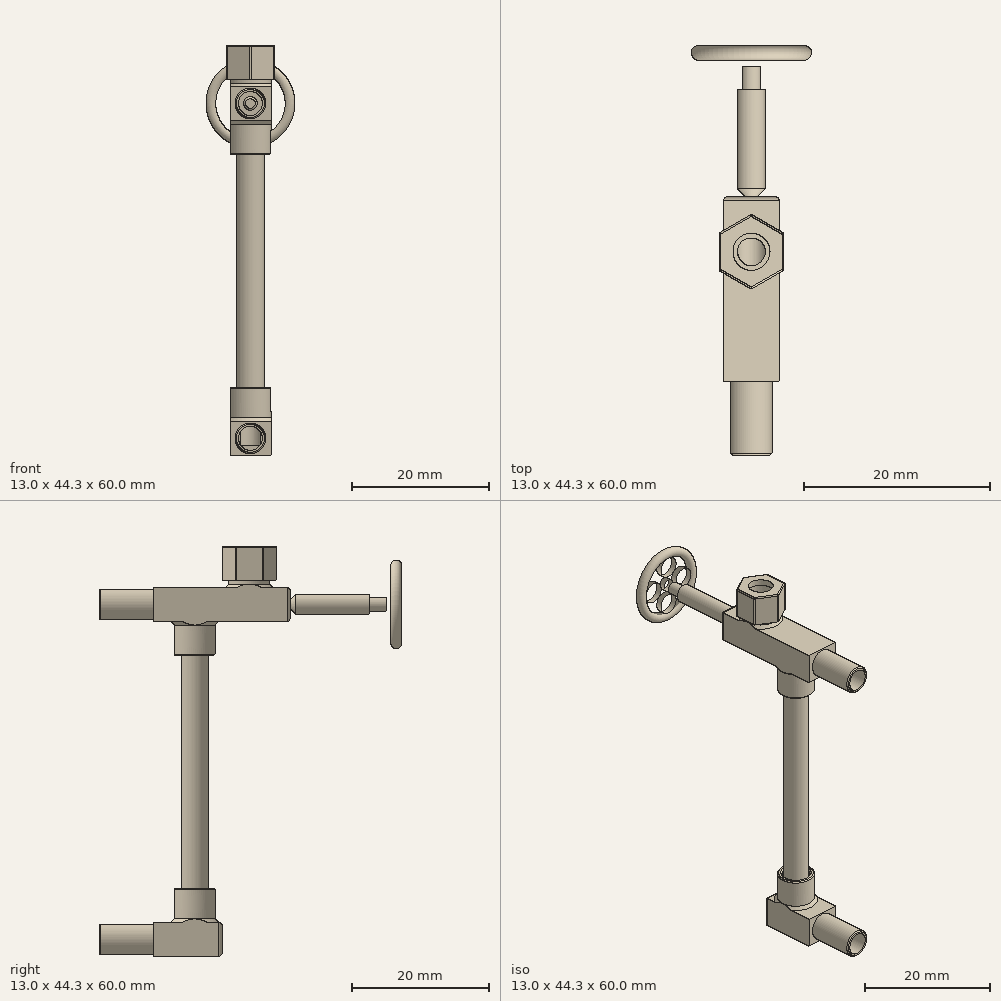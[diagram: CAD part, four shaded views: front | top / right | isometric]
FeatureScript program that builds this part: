
annotation { "Feature Type Name" : "Feature", "Feature Type Description" : "" }
export const myFeature = defineFeature(function(context is Context, id is Id, definition is map)
    precondition{}
    {
        {
            var Q0;
            Q0=qCreatedBy(makeId("Front.planeOp"),FACE);
            var sketch = newSketch(context, id + "F0", { "sketchPlane" : qUnion([Q0])});
            skCircle(sketch, "E0", {"center": v(0, 0) * mm, "radius": 1.75 * mm});
            skCircle(sketch, "E1", {"center": v(0, 0) * mm, "radius": 2.25 * mm});
            skLineSegment(sketch, "E2.rect.bottom", {"start": v(-3, -2.5) * mm, "end": v(3, -2.5) * mm});
            skLineSegment(sketch, "E2.rect.top", {"start": v(-3, 2.5) * mm, "end": v(3, 2.5) * mm});
            skLineSegment(sketch, "E2.rect.left", {"start": v(-3, -2.5) * mm, "end": v(-3, 2.5) * mm});
            skLineSegment(sketch, "E2.rect.right", {"start": v(3, -2.5) * mm, "end": v(3, 2.5) * mm});
            skSolve(sketch);
        }
        {
            var Q0;
            Q0=makeQuery(id+"F0.imprint","IMPRINT",FACE,{"disambiguationData":[TD([[makeQuery(id+"F0.imprint","IMPRINT",EDGE,{"derivedFrom":sQuery(id+"F0.wireOp",EDGE,"E0")}),-1.0]])]});
            var Q1;
            Q1=makeQuery(id+"F0.imprint","IMPRINT",FACE,{"disambiguationData":[TD([[makeQuery(id+"F0.imprint","IMPRINT",EDGE,{"derivedFrom":sQuery(id+"F0.wireOp",EDGE,"E1")}),-1.0]])]});
            var Q2;
            Q2=makeQuery(id+"F0.imprint","IMPRINT",FACE,{"disambiguationData":[TD([[makeQuery(id+"F0.imprint","IMPRINT",EDGE,{"derivedFrom":sQuery(id+"F0.wireOp",EDGE,"E0")}),1.0]])]});
            extrude(context, id + "F1", {"entities" : qUnion([Q0, Q1, Q2]), "oppositeDirection" : true, "depth" : 20 * mm});
        }
        {
            var Q0;
            Q0=makeQuery(id+"F0.imprint","IMPRINT",FACE,{"disambiguationData":[TD([[makeQuery(id+"F0.imprint","IMPRINT",EDGE,{"derivedFrom":sQuery(id+"F0.wireOp",EDGE,"E0")}),-1.0]])]});
            extrude(context, id + "F2", {"entities" : qUnion([Q0]), "operationType" : NewBodyOperationType.ADD, "depth" : 8 * mm});
        }
        {
            var Q0;
            Q0=makeQuery(id+"F0.imprint","IMPRINT",FACE,{"disambiguationData":[TD([[makeQuery(id+"F0.imprint","IMPRINT",EDGE,{"derivedFrom":sQuery(id+"F0.wireOp",EDGE,"E0")}),1.0]])]});
            extrude(context, id + "F3", {"entities" : qUnion([Q0]), "operationType" : NewBodyOperationType.REMOVE, "oppositeDirection" : true, "depth" : 8 * mm});
        }
        {
            var Q0;
            Q0=makeQuery(id+"F1.opExtrude","CAP_FACE",FACE,{"disambiguationData":[OSD([sQuery(id+"F0.wireOp",EDGE,"E2.rect.bottom"),sQuery(id+"F0.wireOp",EDGE,"E2.rect.top"),sQuery(id+"F0.wireOp",EDGE,"E2.rect.left"),sQuery(id+"F0.wireOp",EDGE,"E2.rect.right")])],"isStart":false});
            var sketch = newSketch(context, id + "F4", { "sketchPlane" : qUnion([Q0])});
            skLineSegment(sketch, "E3", {"start": v(0, -2.5) * mm, "end": v(0, 2.5) * mm, "construction": true});
            skCircle(sketch, "E4", {"center": v(0, 0) * mm, "radius": 1.5 * mm});
            skCircle(sketch, "E5", {"center": v(0, 0) * mm, "radius": 1 * mm});
            skSolve(sketch);
        }
        {
            var Q0;
            Q0=makeQuery(id+"F4.imprint","IMPRINT",FACE,{"disambiguationData":[TD([[makeQuery(id+"F4.imprint","IMPRINT",EDGE,{"derivedFrom":sQuery(id+"F4.wireOp",EDGE,"E5")}),1.0]])]});
            extrude(context, id + "F5", {"entities" : qUnion([Q0]), "operationType" : NewBodyOperationType.REMOVE, "oppositeDirection" : true, "depth" : 12 * mm});
        }
        {
            var Q0;
            Q0=makeQuery(id+"F4.imprint","IMPRINT",FACE,{"disambiguationData":[TD([[makeQuery(id+"F4.imprint","IMPRINT",EDGE,{"derivedFrom":sQuery(id+"F4.wireOp",EDGE,"E4")}),1.0]])]});
            extrude(context, id + "F6", {"entities" : qUnion([Q0]), "operationType" : NewBodyOperationType.REMOVE, "oppositeDirection" : true, "depth" : 10 * mm});
        }
        {
            var Q0;
            Q0=makeQuery(id+"F1.opExtrude","SWEPT_FACE",FACE,{"disambiguationData":[OSD([sQuery(id+"F0.wireOp",EDGE,"E2.rect.top")])]});
            var sketch = newSketch(context, id + "F7", { "sketchPlane" : qUnion([Q0])});
            skLineSegment(sketch, "E6", {"start": v(0, 20) * mm, "end": v(0, 14) * mm, "construction": true});
            skCircle(sketch, "E7", {"center": v(0, 14) * mm, "radius": 3 * mm});
            skCircle(sketch, "E8", {"center": v(0, 14) * mm, "radius": 1.5 * mm});
            skCircle(sketch, "E9", {"center": v(0, 14) * mm, "radius": 2.25 * mm});
            skSolve(sketch);
        }
        {
            var Q0;
            Q0=makeQuery(id+"F7.imprint","IMPRINT",FACE,{"disambiguationData":[TD([[makeQuery(id+"F7.imprint","IMPRINT",EDGE,{"derivedFrom":sQuery(id+"F7.wireOp",EDGE,"E8")}),1.0]])]});
            extrude(context, id + "F8", {"entities" : qUnion([Q0]), "operationType" : NewBodyOperationType.REMOVE, "oppositeDirection" : true, "depth" : 2.5 * mm});
        }
        {
            var Q0;
            Q0=makeQuery(id+"F7.imprint","IMPRINT",FACE,{"disambiguationData":[TD([[makeQuery(id+"F7.imprint","IMPRINT",EDGE,{"derivedFrom":sQuery(id+"F7.wireOp",EDGE,"E9")}),-1.0]])]});
            extrude(context, id + "F9", {"entities" : qUnion([Q0]), "operationType" : NewBodyOperationType.ADD, "depth" : 5 * mm});
        }
        {
            var Q0;
            Q0=makeQuery(id+"F1.opExtrude","SWEPT_FACE",FACE,{"disambiguationData":[OSD([sQuery(id+"F0.wireOp",EDGE,"E2.rect.bottom")])]});
            var sketch = newSketch(context, id + "F10", { "sketchPlane" : qUnion([Q0])});
            skLineSegment(sketch, "E10", {"start": v(0, -20) * mm, "end": v(0, -6) * mm, "construction": true});
            skCircle(sketch, "E11", {"center": v(0, -6) * mm, "radius": 3 * mm});
            skCircle(sketch, "E12", {"center": v(0, -6) * mm, "radius": 2.25 * mm});
            skCircle(sketch, "E13", {"center": v(0, -6) * mm, "radius": 1.5 * mm});
            skSolve(sketch);
        }
        {
            var Q0;
            Q0=makeQuery(id+"F10.imprint","IMPRINT",FACE,{"disambiguationData":[TD([[makeQuery(id+"F10.imprint","IMPRINT",EDGE,{"derivedFrom":sQuery(id+"F10.wireOp",EDGE,"E13")}),1.0]])]});
            extrude(context, id + "F11", {"entities" : qUnion([Q0]), "operationType" : NewBodyOperationType.REMOVE, "oppositeDirection" : true, "depth" : 2.5 * mm});
        }
        {
            var Q0;
            Q0=makeQuery(id+"F10.imprint","IMPRINT",FACE,{"disambiguationData":[TD([[makeQuery(id+"F10.imprint","IMPRINT",EDGE,{"derivedFrom":sQuery(id+"F10.wireOp",EDGE,"E12")}),-1.0]])]});
            extrude(context, id + "F12", {"entities" : qUnion([Q0]), "operationType" : NewBodyOperationType.ADD, "depth" : 5 * mm});
        }
        {
            var Q0;
            Q0=makeQuery(id+"F12.boolean.opBoolean","SPLIT",FACE,{"disambiguationData":[TD([makeQuery(id+"F11.boolean.opBoolean","COPY",FACE,{"derivedFrom":makeQuery(id+"F11.opExtrude","SWEPT_FACE",FACE,{"disambiguationData":[OSD([sQuery(id+"F10.wireOp",EDGE,"E13")])]})})])],"derivedFrom":makeQuery(id+"F1.opExtrude","SWEPT_FACE",FACE,{"disambiguationData":[OSD([sQuery(id+"F0.wireOp",EDGE,"E2.rect.bottom")])]})});
            var sketch = newSketch(context, id + "F13", { "sketchPlane" : qUnion([Q0])});
            skCircle(sketch, "E14.0", {"center": v(0, -6) * mm, "radius": 2.25 * mm});
            skCircle(sketch, "E15", {"center": v(0, -6) * mm, "radius": 2 * mm});
            skCircle(sketch, "E16", {"center": v(0, -6) * mm, "radius": 1 * mm});
            skSolve(sketch);
        }
        {
            var Q0;
            Q0=makeQuery(id+"F13.imprint","IMPRINT",FACE,{"disambiguationData":[TD([[makeQuery(id+"F13.imprint","IMPRINT",EDGE,{"derivedFrom":sQuery(id+"F13.wireOp",EDGE,"E15")}),1.0]])]});
            var Q1;
            Q1=makeQuery(id+"F13.imprint","IMPRINT",FACE,{"disambiguationData":[TD([[makeQuery(id+"F13.imprint","IMPRINT",EDGE,{"derivedFrom":sQuery(id+"F13.wireOp",EDGE,"E16")}),-1.0]])]});
            extrude(context, id + "F14", {"entities" : qUnion([Q0, Q1]), "depth" : 44 * mm});
        }
        {
            var Q0;
            Q0=makeQuery(id+"F13.imprint","IMPRINT",FACE,{"disambiguationData":[TD([[makeQuery(id+"F13.imprint","IMPRINT",EDGE,{"derivedFrom":sQuery(id+"F13.wireOp",EDGE,"E14.0")}),1.0]])]});
            extrude(context, id + "F15", {"entities" : qUnion([Q0]), "depth" : 5 * mm});
        }
        {
            var Q0;
            Q0=makeQuery(id+"F9.opExtrude","CAP_FACE",FACE,{"disambiguationData":[OSD([sQuery(id+"F7.wireOp",EDGE,"E7"),sQuery(id+"F7.wireOp",EDGE,"E9")])],"isStart":false});
            var sketch = newSketch(context, id + "F16", { "sketchPlane" : qUnion([Q0])});
            skCircle(sketch, "E17.0", {"center": v(0, 14) * mm, "radius": 3 * mm});
            skCircle(sketch, "E18.cCircle", {"center": v(0, 14) * mm, "radius": 3.5 * mm, "construction": true});
            skLineSegment(sketch, "E18.0", {"start": v(3.5, 16.02) * mm, "end": v(3.5, 11.98) * mm});
            skLineSegment(sketch, "E18.1", {"start": v(3.5, 11.98) * mm, "end": v(0, 9.96) * mm});
            skLineSegment(sketch, "E18.2", {"start": v(0, 9.96) * mm, "end": v(-3.5, 11.98) * mm});
            skLineSegment(sketch, "E18.3", {"start": v(-3.5, 11.98) * mm, "end": v(-3.5, 16.02) * mm});
            skLineSegment(sketch, "E18.4", {"start": v(-3.5, 16.02) * mm, "end": v(0, 18.04) * mm});
            skLineSegment(sketch, "E18.5", {"start": v(0, 18.04) * mm, "end": v(3.5, 16.02) * mm});
            skPoint(sketch, "E18.0.midPoint", {"position": v(3.5, 14) * mm});
            skCircle(sketch, "E19", {"center": v(0, 14) * mm, "radius": 2 * mm});
            skSolve(sketch);
        }
        {
            var Q0;
            Q0=makeQuery(id+"F16.imprint","IMPRINT",FACE,{"disambiguationData":[TD([[makeQuery(id+"F16.imprint","IMPRINT",EDGE,{"derivedFrom":sQuery(id+"F16.wireOp",EDGE,"E17.0")}),-1.0]])]});
            extrude(context, id + "F17", {"entities" : qUnion([Q0]), "oppositeDirection" : true, "depth" : 4 * mm});
        }
        {
            var Q0;
            Q0=makeQuery(id+"F16.imprint","IMPRINT",FACE,{"disambiguationData":[TD([[makeQuery(id+"F16.imprint","IMPRINT",EDGE,{"derivedFrom":sQuery(id+"F16.wireOp",EDGE,"E17.0")}),-1.0]])]});
            var Q1;
            Q1=makeQuery(id+"F16.imprint","IMPRINT",FACE,{"disambiguationData":[TD([[makeQuery(id+"F16.imprint","IMPRINT",EDGE,{"derivedFrom":sQuery(id+"F16.wireOp",EDGE,"E17.0")}),1.0]])]});
            var Q2;
            Q2=makeQuery(id+"F16.imprint","IMPRINT",FACE,{"disambiguationData":[TD([[makeQuery(id+"F16.imprint","IMPRINT",EDGE,{"derivedFrom":sQuery(id+"F16.wireOp",EDGE,"E19")}),-1.0]])]});
            extrude(context, id + "F18", {"entities" : qUnion([Q0, Q1, Q2]), "operationType" : NewBodyOperationType.ADD, "depth" : 1 * mm});
        }
        {
            var Q0;
            Q0=makeQuery(id+"F1.opExtrude","CAP_FACE",FACE,{"disambiguationData":[OSD([sQuery(id+"F0.wireOp",EDGE,"E2.rect.bottom"),sQuery(id+"F0.wireOp",EDGE,"E2.rect.top"),sQuery(id+"F0.wireOp",EDGE,"E2.rect.left"),sQuery(id+"F0.wireOp",EDGE,"E2.rect.right")])],"isStart":false});
            var sketch = newSketch(context, id + "F19", { "sketchPlane" : qUnion([Q0])});
            skCircle(sketch, "E20.0", {"center": v(0, 0) * mm, "radius": 1 * mm});
            skSolve(sketch);
        }
        {
            var Q0;
            Q0=makeQuery(id+"F19.imprint","IMPRINT",FACE,{"disambiguationData":[TD([[makeQuery(id+"F19.imprint","IMPRINT",EDGE,{"derivedFrom":sQuery(id+"F19.wireOp",EDGE,"E20.0")}),1.0]])]});
            extrude(context, id + "F20", {"entities" : qUnion([Q0]), "depth" : 14 * mm});
        }
        {
            var Q0;
            Q0=makeQuery(id+"F19.imprint","IMPRINT",FACE,{"disambiguationData":[TD([[makeQuery(id+"F19.imprint","IMPRINT",EDGE,{"derivedFrom":sQuery(id+"F19.wireOp",EDGE,"E20.0")}),-1.0]])]});
            extrude(context, id + "F21", {"entities" : qUnion([Q0]), "operationType" : NewBodyOperationType.ADD, "depth" : 11.5 * mm});
        }
        {
            var Q0;
            Q0=makeQuery(id+"F21.opExtrude","CAP_EDGE",EDGE,{"disambiguationData":[OSD([sQuery(id+"F4.wireOp",EDGE,"E4")])],"isStart":true});
            chamfer(context, id + "F22", {"entities" : qUnion([Q0]), "width" : 0.8 * mm, "tangentPropagation" : true});
        }
        {
            var Q0;
            Q0=qCreatedBy(makeId("Right.planeOp"),FACE);
            var sketch = newSketch(context, id + "F23", { "sketchPlane" : qUnion([Q0])});
            skLineSegment(sketch, "E21", {"start": v(0, 0) * mm, "end": v(35, 0) * mm, "construction": true});
            skLineSegment(sketch, "E22.bottom", {"start": v(35, 0) * mm, "end": v(36, 0) * mm});
            skLineSegment(sketch, "E22.top", {"start": v(35, 1) * mm, "end": v(36, 1) * mm});
            skLineSegment(sketch, "E22.left", {"start": v(35, 0) * mm, "end": v(35, 1) * mm});
            skLineSegment(sketch, "E22.right", {"start": v(36, 0) * mm, "end": v(36, 1) * mm});
            skLineSegment(sketch, "E23", {"start": v(35.5, 0) * mm, "end": v(35.5, 5.7) * mm, "construction": true});
            skCircle(sketch, "E24", {"center": v(35.5, 5.7) * mm, "radius": 0.8 * mm});
            skLineSegment(sketch, "E25.top", {"start": v(35, 5.08) * mm, "end": v(36, 5.08) * mm});
            skLineSegment(sketch, "E25.left", {"start": v(35, 1) * mm, "end": v(35, 5.08) * mm});
            skLineSegment(sketch, "E25.right", {"start": v(36, 1) * mm, "end": v(36, 5.08) * mm});
            skSolve(sketch);
        }
        {
            var Q0;
            {var subQ0=sQuery(id+"F23.wireOp",EDGE,"E25.top");Q0=makeQuery(id+"F23.imprint","IMPRINT",FACE,{"disambiguationData":[TD([[makeQuery(id+"F23.imprint","IMPRINT",EDGE,{"derivedFrom":subQ0}),-1.0]])]});}
            var Q1;
            {var subQ0=sQuery(id+"F23.wireOp",EDGE,"E25.top");Q1=makeQuery(id+"F23.imprint","IMPRINT",FACE,{"disambiguationData":[TD([[makeQuery(id+"F23.imprint","IMPRINT",EDGE,{"derivedFrom":subQ0}),1.0]])]});}
            var Q2;
            Q2=makeQuery(id+"F23.imprint","IMPRINT",FACE,{"disambiguationData":[TD([[makeQuery(id+"F23.imprint","IMPRINT",EDGE,{"derivedFrom":sQuery(id+"F23.wireOp",EDGE,"E22.top")}),1.0]])]});
            var Q3;
            Q3=sQuery(id+"F23.wireOp",EDGE,"E22.bottom");
            revolve(context, id + "F24", {"entities" : qUnion([Q0, Q1, Q2]), "axis" : qUnion([Q3]), "revolveType" : RevolveType.FULL});
        }
        {
            var Q0;
            Q0=makeQuery(id+"F24.opRevolve","SWEPT_FACE",FACE,{"disambiguationData":[OSD([sQuery(id+"F23.wireOp",EDGE,"E25.right")])]});
            var sketch = newSketch(context, id + "F25", { "sketchPlane" : qUnion([Q0])});
            skCircle(sketch, "E26.0", {"center": v(0, 0) * mm, "radius": 5.08 * mm});
            skLineSegment(sketch, "E27", {"start": v(0, 0) * mm, "end": v(0, 3.38) * mm, "construction": true});
            skCircle(sketch, "E28", {"center": v(0, 3.38) * mm, "radius": 1.7 * mm});
            skSolve(sketch);
        }
        {
            var Q0;
            Q0=makeQuery(id+"F25.imprint","IMPRINT",FACE,{"disambiguationData":[TD([[makeQuery(id+"F25.imprint","IMPRINT",EDGE,{"derivedFrom":sQuery(id+"F25.wireOp",EDGE,"E28")}),1.0]])]});
            extrude(context, id + "F26", {"entities" : qUnion([Q0]), "operationType" : NewBodyOperationType.REMOVE, "oppositeDirection" : true, "depth" : 1 * mm});
        }
        {
            var Q0;
            Q0=makeQuery(id+"F26.boolean.opBoolean","COPY",FACE,{"derivedFrom":makeQuery(id+"F26.opExtrude","SWEPT_FACE",FACE,{"disambiguationData":[OSD([sQuery(id+"F25.wireOp",EDGE,"E28")])]})});
            var Q1;
            Q1=makeQuery(id+"F24.opRevolve","SWEPT_BODY",BODY,{"disambiguationData":[OSD([sQuery(id+"F23.wireOp",EDGE,"E24"),sQuery(id+"F23.wireOp",EDGE,"E22.top"),sQuery(id+"F23.wireOp",EDGE,"E25.left"),sQuery(id+"F23.wireOp",EDGE,"E25.right")])]});
            var Q2;
            Q2=makeQuery(id+"F24.opRevolve","SWEPT_EDGE",EDGE,{"disambiguationData":[OSD([sQuery(id+"F23.wireOp",EDGE,"E22.right"),sQuery(id+"F23.wireOp",EDGE,"E22.top"),sQuery(id+"F23.wireOp",EDGE,"E25.right")])]});
            circularPattern(context, id + "F27", {"faces" : qUnion([Q0]), "axis" : qUnion([Q2]), "angle" : 90 * degree, "instanceCount" : 4, "patternType" : PatternType.FACE});
        }
        {
            var Q0;
            Q0=makeQuery(id+"F14.opExtrude","CAP_FACE",FACE,{"disambiguationData":[OSD([sQuery(id+"F13.wireOp",EDGE,"E15"),sQuery(id+"F13.wireOp",EDGE,"E16")])],"isStart":false});
            var sketch = newSketch(context, id + "F28", { "sketchPlane" : qUnion([Q0])});
            skCircle(sketch, "E29.0", {"center": v(0, -6) * mm, "radius": 3 * mm});
            skCircle(sketch, "E29.1", {"center": v(0, -6) * mm, "radius": 2.25 * mm});
            skLineSegment(sketch, "E29.2", {"start": v(3, -6) * mm, "end": v(3, 0) * mm});
            skLineSegment(sketch, "E30.bottom", {"start": v(3, 0) * mm, "end": v(-3, 0) * mm});
            skLineSegment(sketch, "E30.top", {"start": v(3, -10) * mm, "end": v(-3, -10) * mm});
            skLineSegment(sketch, "E30.left", {"start": v(3, 0) * mm, "end": v(3, -10) * mm});
            skLineSegment(sketch, "E30.right", {"start": v(-3, 0) * mm, "end": v(-3, -10) * mm});
            skCircle(sketch, "E31.0", {"center": v(0, -6) * mm, "radius": 1.5 * mm});
            skSolve(sketch);
        }
        {
            var Q0;
            Q0=makeQuery(id+"F28.imprint","IMPRINT",FACE,{"disambiguationData":[TD([[makeQuery(id+"F28.imprint","IMPRINT",EDGE,{"derivedFrom":sQuery(id+"F28.wireOp",EDGE,"E29.1")}),-1.0]])]});
            extrude(context, id + "F29", {"entities" : qUnion([Q0]), "oppositeDirection" : true, "depth" : 5 * mm});
        }
        {
            var Q0;
            {var subQ3=sQuery(id+"F28.wireOp",EDGE,"E30.top");Q0=makeQuery(id+"F28.imprint","IMPRINT",FACE,{"disambiguationData":[TD([[makeQuery(id+"F28.imprint","IMPRINT",EDGE,{"derivedFrom":subQ3}),-1.0]])]});}
            var Q1;
            Q1=makeQuery(id+"F28.imprint","IMPRINT",FACE,{"disambiguationData":[TD([[makeQuery(id+"F28.imprint","IMPRINT",EDGE,{"derivedFrom":sQuery(id+"F28.wireOp",EDGE,"E29.1")}),-1.0]])]});
            var Q2;
            {var subQ3=sQuery(id+"F28.wireOp",EDGE,"E30.bottom");Q2=makeQuery(id+"F28.imprint","IMPRINT",FACE,{"disambiguationData":[TD([[makeQuery(id+"F28.imprint","IMPRINT",EDGE,{"derivedFrom":subQ3}),1.0]])]});}
            var Q3;
            Q3=makeQuery(id+"F28.imprint","IMPRINT",FACE,{"disambiguationData":[TD([[makeQuery(id+"F28.imprint","IMPRINT",EDGE,{"derivedFrom":makeQuery(id+"F14.opExtrude","CAP_EDGE",EDGE,{"disambiguationData":[OSD([sQuery(id+"F13.wireOp",EDGE,"E16")])],"isStart":false})}),1.0]])]});
            var Q4;
            Q4=makeQuery(id+"F28.imprint","IMPRINT",FACE,{"disambiguationData":[TD([[makeQuery(id+"F28.imprint","IMPRINT",EDGE,{"derivedFrom":sQuery(id+"F28.wireOp",EDGE,"E31.0")}),1.0]])]});
            var Q5;
            Q5=makeQuery(id+"F28.imprint","IMPRINT",FACE,{"disambiguationData":[TD([[makeQuery(id+"F28.imprint","IMPRINT",EDGE,{"derivedFrom":sQuery(id+"F28.wireOp",EDGE,"E31.0")}),-1.0]])]});
            var Q6;
            Q6=makeQuery(id+"F28.imprint","IMPRINT",FACE,{"disambiguationData":[TD([[makeQuery(id+"F28.imprint","IMPRINT",EDGE,{"derivedFrom":sQuery(id+"F28.wireOp",EDGE,"E29.1")}),1.0]])]});
            extrude(context, id + "F30", {"entities" : qUnion([Q0, Q1, Q2, Q3, Q4, Q5, Q6]), "operationType" : NewBodyOperationType.ADD, "depth" : 5 * mm});
        }
        {
            var Q0;
            Q0=makeQuery(id+"F28.imprint","IMPRINT",FACE,{"disambiguationData":[TD([[makeQuery(id+"F28.imprint","IMPRINT",EDGE,{"derivedFrom":makeQuery(id+"F14.opExtrude","CAP_EDGE",EDGE,{"disambiguationData":[OSD([sQuery(id+"F13.wireOp",EDGE,"E16")])],"isStart":false})}),1.0]])]});
            var Q1;
            Q1=makeQuery(id+"F28.imprint","IMPRINT",FACE,{"disambiguationData":[TD([[makeQuery(id+"F28.imprint","IMPRINT",EDGE,{"derivedFrom":sQuery(id+"F28.wireOp",EDGE,"E31.0")}),1.0]])]});
            extrude(context, id + "F31", {"entities" : qUnion([Q0, Q1]), "operationType" : NewBodyOperationType.REMOVE, "depth" : 3.5 * mm});
        }
        {
            var Q0;
            Q0=makeQuery(id+"F30.opExtrude","SWEPT_FACE",FACE,{"disambiguationData":[OSD([sQuery(id+"F28.wireOp",EDGE,"E30.bottom")])]});
            var sketch = newSketch(context, id + "F32", { "sketchPlane" : qUnion([Q0])});
            skLineSegment(sketch, "E32", {"start": v(0, -51.5) * mm, "end": v(0, -46.5) * mm, "construction": true});
            skCircle(sketch, "E33", {"center": v(0, -49) * mm, "radius": 2.25 * mm});
            skCircle(sketch, "E34", {"center": v(0, -49) * mm, "radius": 1.75 * mm});
            skSolve(sketch);
        }
        {
            var Q0;
            Q0=makeQuery(id+"F32.imprint","IMPRINT",FACE,{"disambiguationData":[TD([[makeQuery(id+"F32.imprint","IMPRINT",EDGE,{"derivedFrom":sQuery(id+"F32.wireOp",EDGE,"E34")}),1.0]])]});
            extrude(context, id + "F33", {"entities" : qUnion([Q0]), "operationType" : NewBodyOperationType.REMOVE, "oppositeDirection" : true, "depth" : 6.5 * mm});
        }
        {
            var Q0;
            Q0=makeQuery(id+"F32.imprint","IMPRINT",FACE,{"disambiguationData":[TD([[makeQuery(id+"F32.imprint","IMPRINT",EDGE,{"derivedFrom":sQuery(id+"F32.wireOp",EDGE,"E33")}),1.0]])]});
            extrude(context, id + "F34", {"entities" : qUnion([Q0]), "operationType" : NewBodyOperationType.ADD, "depth" : 8 * mm});
        }
        {
            var Q0;
            Q0=makeQuery(id+"F30.boolean.opBoolean","SPLIT",EDGE,{"disambiguationData":[OD(1.0)],"derivedFrom":makeQuery(id+"F29.opExtrude","CAP_EDGE",EDGE,{"disambiguationData":[OSD([sQuery(id+"F28.wireOp",EDGE,"E29.0")])],"isStart":true})});
            var Q1;
            Q1=makeQuery(id+"F30.boolean.opBoolean","SPLIT",EDGE,{"disambiguationData":[OD(0.0)],"derivedFrom":makeQuery(id+"F29.opExtrude","CAP_EDGE",EDGE,{"disambiguationData":[OSD([sQuery(id+"F28.wireOp",EDGE,"E29.0")])],"isStart":true})});
            chamfer(context, id + "F35", {"entities" : qUnion([Q0, Q1]), "width" : 0.5 * mm, "tangentPropagation" : true});
        }
        {
            var Q0;
            Q0=makeQuery(id+"F30.opExtrude","SWEPT_FACE",FACE,{"disambiguationData":[OSD([sQuery(id+"F28.wireOp",EDGE,"E30.top")])]});
            var Q1;
            Q1=makeQuery(id+"F30.opExtrude","SWEPT_EDGE",EDGE,{"disambiguationData":[OSD([sQuery(id+"F28.wireOp",EDGE,"E30.top"),sQuery(id+"F28.wireOp",EDGE,"E30.left")])]});
            var Q2;
            Q2=makeQuery(id+"F30.opExtrude","CAP_EDGE",EDGE,{"disambiguationData":[OSD([sQuery(id+"F28.wireOp",EDGE,"E30.top")])],"isStart":false});
            fillet(context, id + "F36", {"entities" : qUnion([Q0, Q1, Q2]), "radius" : 0.5 * mm, "tangentPropagation" : true, "allowEdgeOverflow" : false});
        }
        {
            var Q0;
            Q0=makeQuery(id+"F1.opExtrude","CAP_EDGE",EDGE,{"disambiguationData":[OSD([sQuery(id+"F0.wireOp",EDGE,"E2.rect.right")])],"isStart":false});
            var Q1;
            Q1=makeQuery(id+"F1.opExtrude","CAP_EDGE",EDGE,{"disambiguationData":[OSD([sQuery(id+"F0.wireOp",EDGE,"E2.rect.top")])],"isStart":false});
            var Q2;
            Q2=makeQuery(id+"F1.opExtrude","CAP_EDGE",EDGE,{"disambiguationData":[OSD([sQuery(id+"F0.wireOp",EDGE,"E2.rect.bottom")])],"isStart":false});
            var Q3;
            Q3=makeQuery(id+"F1.opExtrude","CAP_EDGE",EDGE,{"disambiguationData":[OSD([sQuery(id+"F0.wireOp",EDGE,"E2.rect.left")])],"isStart":false});
            fillet(context, id + "F37", {"entities" : qUnion([Q0, Q1, Q2, Q3]), "radius" : 0.5 * mm, "tangentPropagation" : true, "allowEdgeOverflow" : false});
        }
        {
            var Q0;
            Q0=makeQuery(id+"F9.boolean.opBoolean","SPLIT",EDGE,{"disambiguationData":[OD(1.0)],"derivedFrom":makeQuery(id+"F9.opExtrude","CAP_EDGE",EDGE,{"disambiguationData":[OSD([sQuery(id+"F7.wireOp",EDGE,"E7")])],"isStart":true})});
            var Q1;
            Q1=makeQuery(id+"F12.boolean.opBoolean","SPLIT",EDGE,{"disambiguationData":[OD(1.0)],"derivedFrom":makeQuery(id+"F12.opExtrude","CAP_EDGE",EDGE,{"disambiguationData":[OSD([sQuery(id+"F10.wireOp",EDGE,"E11")])],"isStart":true})});
            chamfer(context, id + "F38", {"entities" : qUnion([Q0, Q1]), "width" : 0.5 * mm, "tangentPropagation" : true});
        }
        {
            var Q0;
            Q0=makeQuery(id+"F29.opExtrude","CAP_EDGE",EDGE,{"disambiguationData":[OSD([sQuery(id+"F28.wireOp",EDGE,"E29.0")])],"isStart":false});
            var Q1;
            Q1=makeQuery(id+"F9.opExtrude","CAP_EDGE",EDGE,{"disambiguationData":[OSD([sQuery(id+"F7.wireOp",EDGE,"E7")])],"isStart":false});
            var Q2;
            Q2=makeQuery(id+"F12.opExtrude","CAP_EDGE",EDGE,{"disambiguationData":[OSD([sQuery(id+"F10.wireOp",EDGE,"E11")])],"isStart":false});
            var Q3;
            Q3=makeQuery(id+"F34.opExtrude","CAP_EDGE",EDGE,{"disambiguationData":[OSD([sQuery(id+"F32.wireOp",EDGE,"E33")])],"isStart":false});
            var Q4;
            Q4=makeQuery(id+"F2.opExtrude","CAP_EDGE",EDGE,{"disambiguationData":[OSD([sQuery(id+"F0.wireOp",EDGE,"E1")])],"isStart":false});
            var Q5;
            Q5=makeQuery(id+"F29.opExtrude","CAP_EDGE",EDGE,{"disambiguationData":[OSD([sQuery(id+"F28.wireOp",EDGE,"E29.1")])],"isStart":false});
            var Q6;
            Q6=makeQuery(id+"F12.opExtrude","CAP_EDGE",EDGE,{"disambiguationData":[OSD([sQuery(id+"F10.wireOp",EDGE,"E12")])],"isStart":false});
            chamfer(context, id + "F39", {"entities" : qUnion([Q0, Q1, Q2, Q3, Q4, Q5, Q6]), "width" : 0.2 * mm, "tangentPropagation" : true});
        }
        {
            var Q0;
            {var subQ0=sQuery(id+"F16.wireOp",EDGE,"E18.0");var subQ1=sQuery(id+"F16.wireOp",EDGE,"E18.5");Q0=makeQuery(id+"F18.boolean.opBoolean","MERGE",EDGE,{"derivedFrom":[makeQuery(id+"F17.opExtrude","SWEPT_EDGE",EDGE,{"disambiguationData":[OSD([subQ0,subQ1])]}),makeQuery(id+"F18.opExtrude","SWEPT_EDGE",EDGE,{"disambiguationData":[OSD([subQ0,subQ1])]})]});}
            var Q1;
            {var subQ0=sQuery(id+"F16.wireOp",EDGE,"E18.4");var subQ1=sQuery(id+"F16.wireOp",EDGE,"E18.5");Q1=makeQuery(id+"F18.boolean.opBoolean","MERGE",EDGE,{"derivedFrom":[makeQuery(id+"F17.opExtrude","SWEPT_EDGE",EDGE,{"disambiguationData":[OSD([subQ0,subQ1])]}),makeQuery(id+"F18.opExtrude","SWEPT_EDGE",EDGE,{"disambiguationData":[OSD([subQ0,subQ1])]})]});}
            var Q2;
            {var subQ0=sQuery(id+"F16.wireOp",EDGE,"E18.3");var subQ1=sQuery(id+"F16.wireOp",EDGE,"E18.4");Q2=makeQuery(id+"F18.boolean.opBoolean","MERGE",EDGE,{"derivedFrom":[makeQuery(id+"F17.opExtrude","SWEPT_EDGE",EDGE,{"disambiguationData":[OSD([subQ0,subQ1])]}),makeQuery(id+"F18.opExtrude","SWEPT_EDGE",EDGE,{"disambiguationData":[OSD([subQ0,subQ1])]})]});}
            var Q3;
            {var subQ0=sQuery(id+"F16.wireOp",EDGE,"E18.0");var subQ1=sQuery(id+"F16.wireOp",EDGE,"E18.1");Q3=makeQuery(id+"F18.boolean.opBoolean","MERGE",EDGE,{"derivedFrom":[makeQuery(id+"F17.opExtrude","SWEPT_EDGE",EDGE,{"disambiguationData":[OSD([subQ0,subQ1])]}),makeQuery(id+"F18.opExtrude","SWEPT_EDGE",EDGE,{"disambiguationData":[OSD([subQ0,subQ1])]})]});}
            var Q4;
            {var subQ0=sQuery(id+"F16.wireOp",EDGE,"E18.2");var subQ1=sQuery(id+"F16.wireOp",EDGE,"E18.3");Q4=makeQuery(id+"F18.boolean.opBoolean","MERGE",EDGE,{"derivedFrom":[makeQuery(id+"F17.opExtrude","SWEPT_EDGE",EDGE,{"disambiguationData":[OSD([subQ0,subQ1])]}),makeQuery(id+"F18.opExtrude","SWEPT_EDGE",EDGE,{"disambiguationData":[OSD([subQ0,subQ1])]})]});}
            var Q5;
            {var subQ0=sQuery(id+"F16.wireOp",EDGE,"E18.1");var subQ1=sQuery(id+"F16.wireOp",EDGE,"E18.2");Q5=makeQuery(id+"F18.boolean.opBoolean","MERGE",EDGE,{"derivedFrom":[makeQuery(id+"F17.opExtrude","SWEPT_EDGE",EDGE,{"disambiguationData":[OSD([subQ0,subQ1])]}),makeQuery(id+"F18.opExtrude","SWEPT_EDGE",EDGE,{"disambiguationData":[OSD([subQ0,subQ1])]})]});}
            var Q6;
            Q6=makeQuery(id+"F18.opExtrude","CAP_EDGE",EDGE,{"disambiguationData":[OSD([sQuery(id+"F16.wireOp",EDGE,"E18.2")])],"isStart":false});
            var Q7;
            Q7=makeQuery(id+"F18.opExtrude","CAP_EDGE",EDGE,{"disambiguationData":[OSD([sQuery(id+"F16.wireOp",EDGE,"E18.1")])],"isStart":false});
            var Q8;
            Q8=makeQuery(id+"F18.opExtrude","CAP_EDGE",EDGE,{"disambiguationData":[OSD([sQuery(id+"F16.wireOp",EDGE,"E18.0")])],"isStart":false});
            var Q9;
            Q9=makeQuery(id+"F18.opExtrude","CAP_EDGE",EDGE,{"disambiguationData":[OSD([sQuery(id+"F16.wireOp",EDGE,"E18.5")])],"isStart":false});
            var Q10;
            Q10=makeQuery(id+"F18.opExtrude","CAP_EDGE",EDGE,{"disambiguationData":[OSD([sQuery(id+"F16.wireOp",EDGE,"E18.4")])],"isStart":false});
            var Q11;
            Q11=makeQuery(id+"F18.opExtrude","CAP_EDGE",EDGE,{"disambiguationData":[OSD([sQuery(id+"F16.wireOp",EDGE,"E18.3")])],"isStart":false});
            fillet(context, id + "F40", {"entities" : qUnion([Q0, Q1, Q2, Q3, Q4, Q5, Q6, Q7, Q8, Q9, Q10, Q11]), "radius" : 0.2 * mm, "tangentPropagation" : true, "allowEdgeOverflow" : false});
        }
    });
